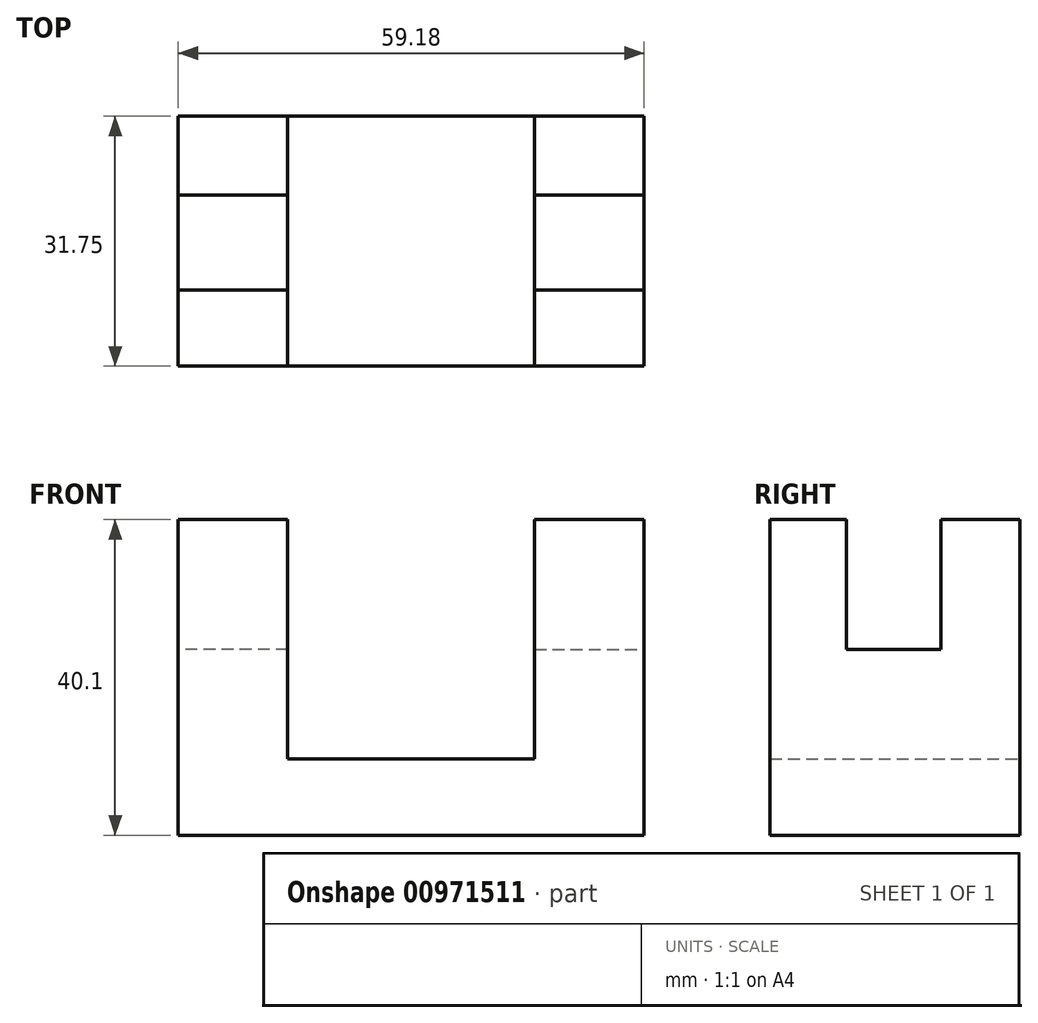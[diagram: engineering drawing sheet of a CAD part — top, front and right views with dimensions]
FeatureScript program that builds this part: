
annotation { "Feature Type Name" : "Feature", "Feature Type Description" : "" }
export const myFeature = defineFeature(function(context is Context, id is Id, definition is map)
    precondition{}
    {
        {
            var Q0;
            Q0=qCreatedBy(makeId("Front.planeOp"),FACE);
            var sketch = newSketch(context, id + "F0", { "sketchPlane" : qUnion([Q0])});
            skLineSegment(sketch, "E0.bottom", {"start": v(0, 0) * mm, "end": v(59.18, 0) * mm});
            skLineSegment(sketch, "E0.top", {"start": v(0, 40.1) * mm, "end": v(13.92, 40.1) * mm});
            skLineSegment(sketch, "E0.left", {"start": v(0, 0) * mm, "end": v(0, 40.1) * mm});
            skLineSegment(sketch, "E0.right", {"start": v(59.18, 0) * mm, "end": v(59.18, 40.1) * mm});
            skLineSegment(sketch, "E1.bottom", {"start": v(45.26, 9.68) * mm, "end": v(13.92, 9.68) * mm});
            skLineSegment(sketch, "E1.left", {"start": v(45.26, 9.68) * mm, "end": v(45.26, 40.1) * mm});
            skLineSegment(sketch, "E1.right", {"start": v(13.92, 9.68) * mm, "end": v(13.92, 40.1) * mm});
            skLineSegment(sketch, "E2.trimOffspring", {"start": v(45.26, 40.1) * mm, "end": v(59.18, 40.1) * mm});
            skSolve(sketch);
        }
        {
            var Q0;
            Q0 = qSketchRegion(id + "F0", true);
            extrude(context, id + "F1", {"entities" : qUnion([Q0]), "depth" : 31.75 * mm, "offsetDistance" : 25.4 * mm});
        }
        {
            var Q0;
            Q0=makeQuery(id+"F1.opExtrude","SWEPT_FACE",FACE,{"disambiguationData":[OSD([sQuery(id+"F0.wireOp",EDGE,"E2.trimOffspring")])]});
            var sketch = newSketch(context, id + "F2", { "sketchPlane" : qUnion([Q0])});
            skLineSegment(sketch, "E3.bottom", {"start": v(45.26, -10.02) * mm, "end": v(59.6, -10.02) * mm});
            skLineSegment(sketch, "E3.top", {"start": v(45.26, -22.05) * mm, "end": v(59.6, -22.05) * mm});
            skLineSegment(sketch, "E3.left", {"start": v(45.26, -10.02) * mm, "end": v(45.26, -22.05) * mm});
            skLineSegment(sketch, "E3.right", {"start": v(59.6, -10.02) * mm, "end": v(59.6, -22.05) * mm});
            skPoint(sketch, "E3.middle", {"position": v(52.43, -16.04) * mm});
            skLineSegment(sketch, "E4", {"start": v(29.7, 0) * mm, "end": v(29.7, -31.43) * mm, "construction": true});
            skLineSegment(sketch, "E5.0", {"start": v(45.26, 0) * mm, "end": v(13.92, 0) * mm});
            skLineSegment(sketch, "E6.0", {"start": v(0, 0) * mm, "end": v(13.92, 0) * mm});
            skLineSegment(sketch, "E7.MirrorCS", {"start": v(14.13, -10.02) * mm, "end": v(14.13, -22.05) * mm});
            skLineSegment(sketch, "E8.MirrorCS", {"start": v(14.13, -22.05) * mm, "end": v(-0.22, -22.05) * mm});
            skLineSegment(sketch, "E9.MirrorCS", {"start": v(-0.22, -10.02) * mm, "end": v(-0.22, -22.05) * mm});
            skLineSegment(sketch, "E10.MirrorCS", {"start": v(14.13, -10.02) * mm, "end": v(-0.22, -10.02) * mm});
            skSolve(sketch);
        }
        {
            var Q0;
            Q0 = qSketchRegion(id + "F2", true);
            extrude(context, id + "F3", {"entities" : qUnion([Q0]), "operationType" : NewBodyOperationType.REMOVE, "oppositeDirection" : true, "depth" : 16.5 * mm, "offsetDistance" : 25.4 * mm});
        }
    });
